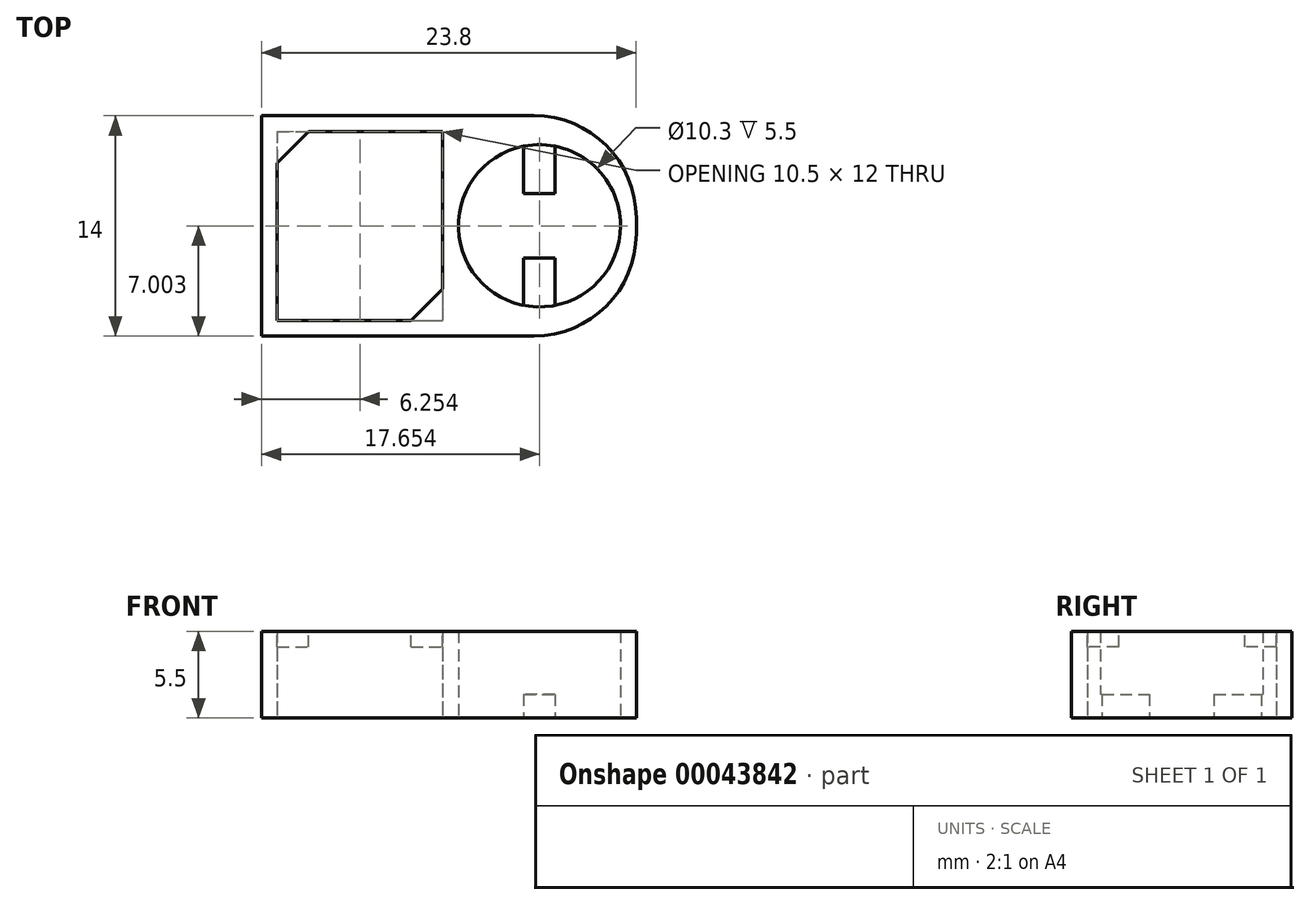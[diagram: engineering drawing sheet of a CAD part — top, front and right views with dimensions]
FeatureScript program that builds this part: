
annotation { "Feature Type Name" : "Feature", "Feature Type Description" : "" }
export const myFeature = defineFeature(function(context is Context, id is Id, definition is map)
    precondition{}
    {
        {
            var Q0;
            Q0=qCreatedBy(makeId("Top.planeOp"),FACE);
            var sketch = newSketch(context, id + "F0", { "sketchPlane" : qUnion([Q0])});
            skPoint(sketch, "E0", {"position": v(0.31, 2.6) * mm});
            skLineSegment(sketch, "E1", {"start": v(5.46, 7.75) * mm, "end": v(5.46, -2.55) * mm, "construction": true});
            skLineSegment(sketch, "E2.top", {"start": v(-12.19, -4.4) * mm, "end": v(11.61, -4.4) * mm});
            skLineSegment(sketch, "E3", {"start": v(6.46, 4.66) * mm, "end": v(6.46, 7.66) * mm});
            skLineSegment(sketch, "E4", {"start": v(-12.19, 2.6) * mm, "end": v(11.61, 2.6) * mm, "construction": true});
            skLineSegment(sketch, "E5", {"start": v(4.46, -2.45) * mm, "end": v(4.46, 0.55) * mm});
            skCircle(sketch, "E6", {"center": v(5.46, 2.6) * mm, "radius": 5.15 * mm});
            skLineSegment(sketch, "E7", {"start": v(6.46, 0.55) * mm, "end": v(6.46, -2.45) * mm});
            skLineSegment(sketch, "E8", {"start": v(4.46, 7.66) * mm, "end": v(4.46, 4.66) * mm});
            skLineSegment(sketch, "E2.bottom", {"start": v(-12.19, 9.6) * mm, "end": v(11.61, 9.6) * mm});
            skLineSegment(sketch, "E9", {"start": v(4.46, 0.55) * mm, "end": v(6.46, 0.55) * mm});
            skLineSegment(sketch, "E10", {"start": v(4.46, 4.66) * mm, "end": v(6.46, 4.66) * mm});
            skLineSegment(sketch, "E2.right", {"start": v(11.61, 9.6) * mm, "end": v(11.61, -4.4) * mm});
            skLineSegment(sketch, "E11", {"start": v(-12.19, 9.6) * mm, "end": v(-12.19, -4.4) * mm});
            skLineSegment(sketch, "E12.bottom", {"start": v(-11.19, 8.6) * mm, "end": v(-0.69, 8.6) * mm});
            skLineSegment(sketch, "E12.top", {"start": v(-11.19, -3.4) * mm, "end": v(-0.69, -3.4) * mm});
            skLineSegment(sketch, "E12.left", {"start": v(-11.19, 8.6) * mm, "end": v(-11.19, -3.4) * mm});
            skLineSegment(sketch, "E12.right", {"start": v(-0.69, 8.6) * mm, "end": v(-0.69, -3.4) * mm});
            skPoint(sketch, "E13", {"position": v(-0.69, 2.6) * mm});
            skPoint(sketch, "E14", {"position": v(-5.94, -3.4) * mm});
            skLineSegment(sketch, "E15", {"start": v(-5.94, 8.6) * mm, "end": v(-5.94, -3.4) * mm, "construction": true});
            skPoint(sketch, "E16", {"position": v(-5.94, 2.6) * mm});
            skSolve(sketch);
        }
        {
            var Q0;
            Q0=makeQuery(id+"F0.imprint","IMPRINT",FACE,{"disambiguationData":[TD([[makeQuery(id+"F0.imprint","IMPRINT",EDGE,{"derivedFrom":sQuery(id+"F0.wireOp",EDGE,"E2.top")}),1.0]])]});
            extrude(context, id + "F1", {"entities" : qUnion([Q0]), "depth" : 5.5 * mm});
        }
        {
            var Q0;
            {var subQ2=sQuery(id+"F0.wireOp",EDGE,"E3");Q0=makeQuery(id+"F0.imprint","IMPRINT",FACE,{"disambiguationData":[TD([[makeQuery(id+"F0.imprint","IMPRINT",EDGE,{"derivedFrom":subQ2}),1.0]])]});}
            var Q1;
            {var subQ2=sQuery(id+"F0.wireOp",EDGE,"E5");Q1=makeQuery(id+"F0.imprint","IMPRINT",FACE,{"disambiguationData":[TD([[makeQuery(id+"F0.imprint","IMPRINT",EDGE,{"derivedFrom":subQ2}),-1.0]])]});}
            extrude(context, id + "F2", {"entities" : qUnion([Q0, Q1]), "operationType" : NewBodyOperationType.ADD, "depth" : 1.5 * mm});
        }
        {
            var Q0;
            Q0=makeQuery(id+"F1.opExtrude","CAP_FACE",FACE,{"disambiguationData":[OSD([sQuery(id+"F0.wireOp",EDGE,"E2.top"),sQuery(id+"F0.wireOp",EDGE,"E6"),sQuery(id+"F0.wireOp",EDGE,"E2.bottom"),sQuery(id+"F0.wireOp",EDGE,"E2.right"),sQuery(id+"F0.wireOp",EDGE,"E11"),sQuery(id+"F0.wireOp",EDGE,"E12.bottom"),sQuery(id+"F0.wireOp",EDGE,"E12.top"),sQuery(id+"F0.wireOp",EDGE,"E12.left"),sQuery(id+"F0.wireOp",EDGE,"E12.right")])],"isStart":false});
            var sketch = newSketch(context, id + "F3", { "sketchPlane" : qUnion([Q0])});
            skLineSegment(sketch, "E17", {"start": v(-11.19, 8.6) * mm, "end": v(-9.19, 8.6) * mm});
            skLineSegment(sketch, "E18", {"start": v(-9.19, 8.6) * mm, "end": v(-11.19, 6.6) * mm});
            skLineSegment(sketch, "E19", {"start": v(-11.19, 6.6) * mm, "end": v(-11.19, 8.6) * mm});
            skLineSegment(sketch, "E20", {"start": v(-0.69, -1.4) * mm, "end": v(-2.69, -3.4) * mm});
            skLineSegment(sketch, "E21", {"start": v(-2.69, -3.4) * mm, "end": v(-0.69, -3.4) * mm});
            skLineSegment(sketch, "E22", {"start": v(-0.69, -3.4) * mm, "end": v(-0.69, -1.4) * mm});
            skSolve(sketch);
        }
        {
            var Q0;
            Q0=makeQuery(id+"F3.imprint","IMPRINT",FACE,{"disambiguationData":[TD([[makeQuery(id+"F3.imprint","IMPRINT",EDGE,{"derivedFrom":sQuery(id+"F3.wireOp",EDGE,"E17")}),-1.0]])]});
            var Q1;
            Q1=makeQuery(id+"F3.imprint","IMPRINT",FACE,{"disambiguationData":[TD([[makeQuery(id+"F3.imprint","IMPRINT",EDGE,{"derivedFrom":sQuery(id+"F3.wireOp",EDGE,"E20")}),1.0]])]});
            extrude(context, id + "F4", {"entities" : qUnion([Q0, Q1]), "operationType" : NewBodyOperationType.ADD, "oppositeDirection" : true, "depth" : 1 * mm});
        }
        {
            var Q0;
            Q0=makeQuery(id+"F1.opExtrude","SWEPT_EDGE",EDGE,{"disambiguationData":[OSD([sQuery(id+"F0.wireOp",EDGE,"E2.bottom"),sQuery(id+"F0.wireOp",EDGE,"E2.right")])]});
            var Q1;
            Q1=makeQuery(id+"F1.opExtrude","SWEPT_EDGE",EDGE,{"disambiguationData":[OSD([sQuery(id+"F0.wireOp",EDGE,"E2.top"),sQuery(id+"F0.wireOp",EDGE,"E2.right")])]});
            fillet(context, id + "F5", {"entities" : qUnion([Q0, Q1]), "radius" : 6.5 * mm, "tangentPropagation" : true, "allowEdgeOverflow" : false});
        }
    });
